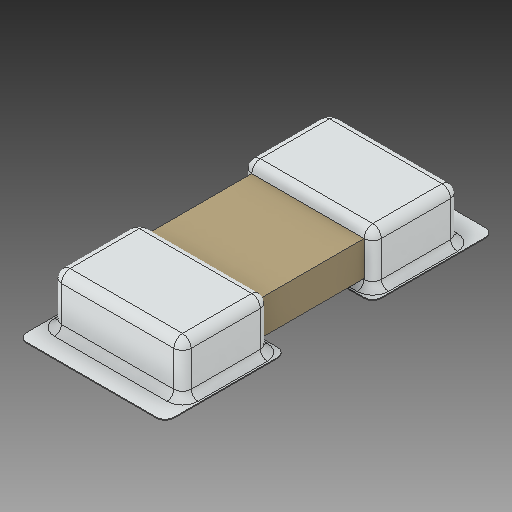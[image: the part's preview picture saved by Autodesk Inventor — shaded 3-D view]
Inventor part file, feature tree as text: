
AUTODESK INVENTOR PART (.ipt)
format: ipt  version: 2019 (Build 230136000, 136)  size: 172,544 bytes
history: native  units: in
note: dims shown in document units (in); Inventor stores cm internally (conversion verified against a paired STEP export)
features: fillet x1
ambient origin geometry x8: Origin, YZ Plane, XZ Plane, XY Plane, X Axis, Y Axis, Z Axis, Center Point
bodies: Solid1 (feature_tree)
feature tree (1):
  fillet  "Fillet2"  [1 undecoded]
note: 1 required parameter value undecoded (feature->parameter linkage not recoverable at this tier; creation-order binding heuristic only, values carry confidence <= 0.55)
